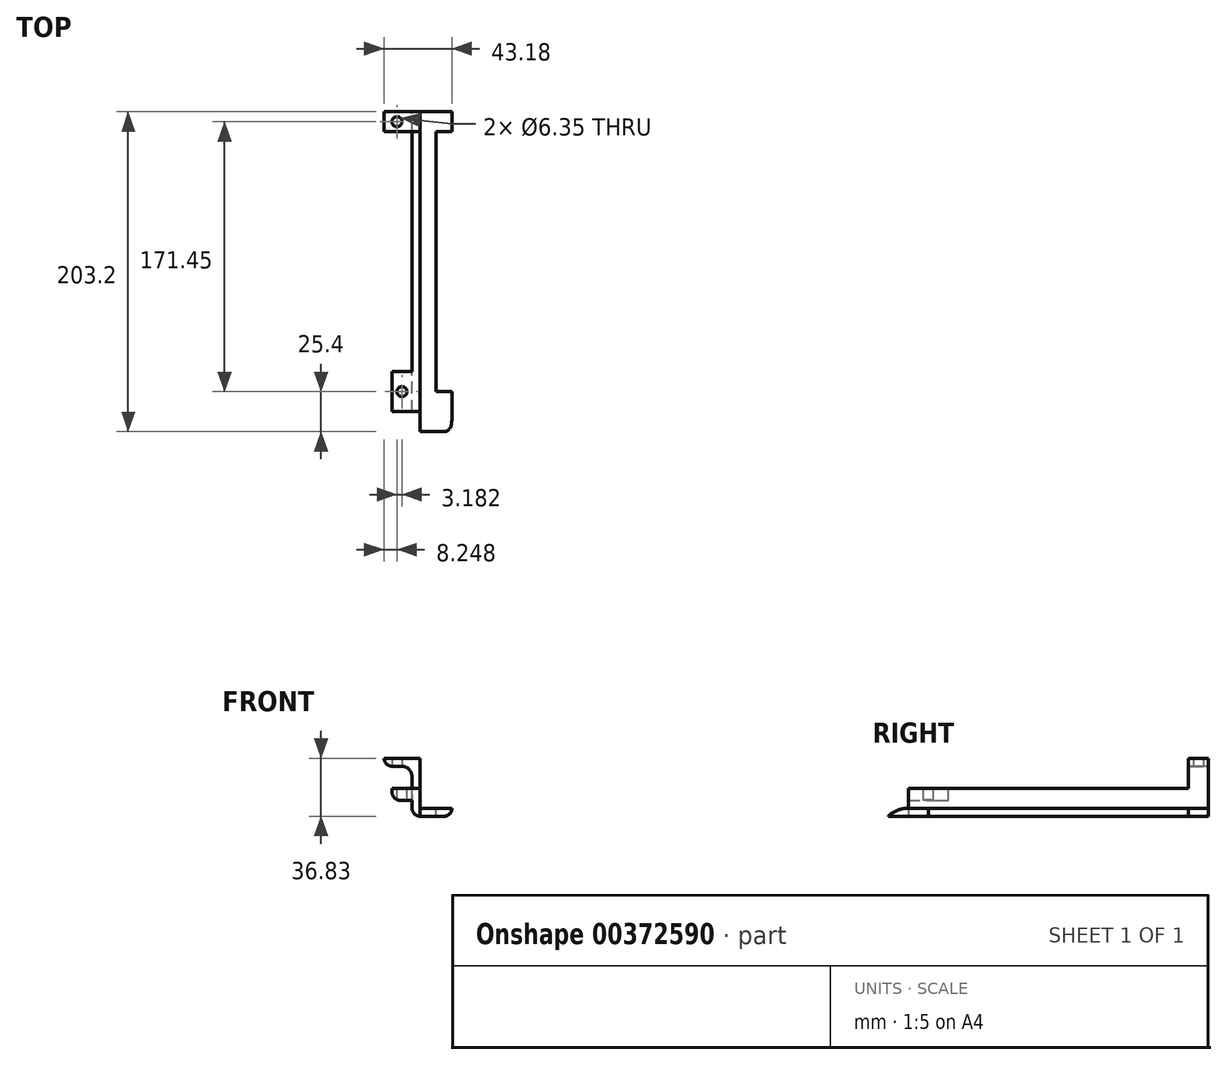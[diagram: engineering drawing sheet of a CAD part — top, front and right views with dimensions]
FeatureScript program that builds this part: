
annotation { "Feature Type Name" : "Feature", "Feature Type Description" : "" }
export const myFeature = defineFeature(function(context is Context, id is Id, definition is map)
    precondition{}
    {
        {
            var Q0;
            Q0=qCreatedBy(makeId("Right.planeOp"),FACE);
            var sketch = newSketch(context, id + "F0", { "sketchPlane" : qUnion([Q0])});
            skLineSegment(sketch, "E0", {"start": v(0, 0) * mm, "end": v(95.25, 0) * mm});
            skLineSegment(sketch, "E1", {"start": v(0, -12.7) * mm, "end": v(0, -6.35) * mm});
            skLineSegment(sketch, "E2", {"start": v(0, -12.7) * mm, "end": v(0, -17.78) * mm});
            skLineSegment(sketch, "E3", {"start": v(0, -17.78) * mm, "end": v(95.25, -17.78) * mm});
            skLineSegment(sketch, "E4", {"start": v(0, -12.7) * mm, "end": v(95.25, -12.7) * mm});
            skLineSegment(sketch, "E5", {"start": v(0, 0) * mm, "end": v(0, -6.35) * mm});
            skLineSegment(sketch, "E6", {"start": v(0, -25.4) * mm, "end": v(0, -12.7) * mm});
            skPoint(sketch, "E7.visualSharp", {"position": v(0, -6.35) * mm});
            skLineSegment(sketch, "E8", {"start": v(95.25, 0) * mm, "end": v(95.25, -17.78) * mm});
            skLineSegment(sketch, "E9.MirrorCS", {"start": v(190.5, 0) * mm, "end": v(95.25, 0) * mm});
            skLineSegment(sketch, "E10.MirrorCS", {"start": v(190.5, 0) * mm, "end": v(190.5, -6.35) * mm});
            skLineSegment(sketch, "E11.MirrorCS", {"start": v(190.5, -12.7) * mm, "end": v(190.5, -6.35) * mm});
            skLineSegment(sketch, "E12.MirrorCS", {"start": v(190.5, -12.7) * mm, "end": v(95.25, -12.7) * mm});
            skLineSegment(sketch, "E13.MirrorCS", {"start": v(190.5, -12.7) * mm, "end": v(190.5, -17.78) * mm});
            skLineSegment(sketch, "E14.MirrorCS", {"start": v(190.5, -17.78) * mm, "end": v(95.25, -17.78) * mm});
            skPoint(sketch, "E15.MirrorCS.start.orphan", {"position": v(190.5, 0) * mm});
            skPoint(sketch, "E16.MirrorCS.start.orphan", {"position": v(190.5, -25.4) * mm});
            skSolve(sketch);
        }
        {
            var Q0;
            {var subQ2=sQuery(id+"F0.wireOp",EDGE,"E0");Q0=makeQuery(id+"F0.imprint","IMPRINT",FACE,{"disambiguationData":[TD([[makeQuery(id+"F0.imprint","IMPRINT",EDGE,{"derivedFrom":subQ2}),-1.0]])]});}
            var Q1;
            Q1=makeQuery(id+"F0.imprint","IMPRINT",FACE,{"disambiguationData":[TD([[makeQuery(id+"F0.imprint","IMPRINT",EDGE,{"derivedFrom":sQuery(id+"F0.wireOp",EDGE,"E1")}),1.0]])]});
            var Q2;
            {var subQ0=sQuery(id+"F0.wireOp",EDGE,"E9.MirrorCS");Q2=makeQuery(id+"F0.imprint","IMPRINT",FACE,{"disambiguationData":[TD([[makeQuery(id+"F0.imprint","IMPRINT",EDGE,{"derivedFrom":subQ0}),1.0]])]});}
            var Q3;
            Q3=makeQuery(id+"F0.imprint","IMPRINT",FACE,{"disambiguationData":[TD([[makeQuery(id+"F0.imprint","IMPRINT",EDGE,{"derivedFrom":sQuery(id+"F0.wireOp",EDGE,"E15.MirrorCS")}),-1.0]])]});
            extrude(context, id + "F1", {"entities" : qUnion([Q0, Q1, Q2, Q3]), "depth" : 5.08 * mm});
        }
        {
            var Q0;
            Q0=makeQuery(id+"F0.imprint","IMPRINT",FACE,{"disambiguationData":[TD([[makeQuery(id+"F0.imprint","IMPRINT",EDGE,{"derivedFrom":sQuery(id+"F0.wireOp",EDGE,"E2")}),1.0]])]});
            var Q1;
            {var subQ2=sQuery(id+"F0.wireOp",EDGE,"E12.MirrorCS");Q1=makeQuery(id+"F0.imprint","IMPRINT",FACE,{"disambiguationData":[TD([[makeQuery(id+"F0.imprint","IMPRINT",EDGE,{"derivedFrom":subQ2}),1.0]])]});}
            var Q2;
            {var subQ0=sQuery(id+"F0.wireOp",EDGE,"E3");Q2=makeQuery(id+"F0.imprint","IMPRINT",FACE,{"disambiguationData":[TD([[makeQuery(id+"F0.imprint","IMPRINT",EDGE,{"derivedFrom":subQ0}),1.0]])]});}
            extrude(context, id + "F2", {"entities" : qUnion([Q0, Q1, Q2]), "operationType" : NewBodyOperationType.ADD, "depth" : 25.4 * mm});
        }
        {
            var Q0;
            {var subQ1=sQuery(id+"F0.wireOp",EDGE,"E0");Q0=makeQuery(id+"F0.imprint","IMPRINT",FACE,{"disambiguationData":[TD([[makeQuery(id+"F0.imprint","IMPRINT",EDGE,{"derivedFrom":subQ1}),-1.0]])]});}
            var sketch = newSketch(context, id + "F3", { "sketchPlane" : qUnion([Q0])});
            skLineSegment(sketch, "E17.bottom", {"start": v(0, 0) * mm, "end": v(50.8, 0) * mm});
            skLineSegment(sketch, "E17.top", {"start": v(0, -7.62) * mm, "end": v(50.8, -7.62) * mm});
            skLineSegment(sketch, "E17.left", {"start": v(0, 0) * mm, "end": v(0, -7.62) * mm});
            skLineSegment(sketch, "E17.right", {"start": v(50.8, 0) * mm, "end": v(50.8, -7.62) * mm});
            skSolve(sketch);
        }
        {
            var Q0;
            Q0=makeQuery(id+"F3.imprint","IMPRINT",FACE,{"disambiguationData":[TD([[makeQuery(id+"F3.imprint","IMPRINT",EDGE,{"derivedFrom":sQuery(id+"F3.wireOp",EDGE,"E17.bottom")}),-1.0]])]});
            extrude(context, id + "F4", {"entities" : qUnion([Q0]), "operationType" : NewBodyOperationType.ADD, "oppositeDirection" : true, "depth" : 12.7 * mm});
        }
        {
            var Q0;
            Q0=makeQuery(id+"F2.opExtrude","CAP_EDGE",EDGE,{"disambiguationData":[OSD([sQuery(id+"F0.wireOp",EDGE,"E3"),sQuery(id+"F0.wireOp",EDGE,"E14.MirrorCS")])],"isStart":true});
            var Q1;
            Q1=makeQuery(id+"F2.opExtrude","CAP_EDGE",EDGE,{"disambiguationData":[OSD([sQuery(id+"F0.wireOp",EDGE,"E3"),sQuery(id+"F0.wireOp",EDGE,"E14.MirrorCS")])],"isStart":false});
            var Q2;
            Q2=makeQuery(id+"F4.opExtrude","CAP_EDGE",EDGE,{"disambiguationData":[OSD([sQuery(id+"F3.wireOp",EDGE,"E17.top")])],"isStart":false});
            fillet(context, id + "F5", {"entities" : qUnion([Q0, Q1, Q2]), "radius" : 5.08 * mm, "tangentPropagation" : true, "allowEdgeOverflow" : false});
        }
        {
            var Q0;
            Q0=makeQuery(id+"F4.boolean.opBoolean","MERGE",FACE,{"derivedFrom":[makeQuery(id+"F1.opExtrude","SWEPT_FACE",FACE,{"disambiguationData":[OSD([sQuery(id+"F0.wireOp",EDGE,"E0"),sQuery(id+"F0.wireOp",EDGE,"E9.MirrorCS")])]}),makeQuery(id+"F4.opExtrude","SWEPT_FACE",FACE,{"disambiguationData":[OSD([sQuery(id+"F3.wireOp",EDGE,"E17.bottom")])]})]});
            var sketch = newSketch(context, id + "F6", { "sketchPlane" : qUnion([Q0])});
            skLineSegment(sketch, "E18", {"start": v(5.08, 0) * mm, "end": v(-12.7, 0) * mm});
            skLineSegment(sketch, "E19", {"start": v(-12.7, 0) * mm, "end": v(0, 0) * mm});
            skLineSegment(sketch, "E20", {"start": v(0, 0) * mm, "end": v(0, 50.8) * mm});
            skLineSegment(sketch, "E21", {"start": v(0, 50.8) * mm, "end": v(-12.7, 50.8) * mm});
            skLineSegment(sketch, "E22", {"start": v(-6.35, 50.8) * mm, "end": v(-6.35, 0) * mm});
            skLineSegment(sketch, "E23", {"start": v(-6.35, 25.4) * mm, "end": v(0, 25.4) * mm});
            skLineSegment(sketch, "E24", {"start": v(-6.35, 25.4) * mm, "end": v(-6.35, 0) * mm});
            skLineSegment(sketch, "E25", {"start": v(-6.35, 25.4) * mm, "end": v(-6.35, 38.1) * mm});
            skPoint(sketch, "E26", {"position": v(-6.35, 38.1) * mm});
            skPoint(sketch, "E27", {"position": v(-6.35, 12.7) * mm});
            skLineSegment(sketch, "E28", {"start": v(-6.35, 25.4) * mm, "end": v(-12.7, 25.4) * mm});
            skSolve(sketch);
        }
        {
            var Q0;
            Q0=sQuery(id+"F6.wireOp",VERTEX,"E27");
            var Q1;
            Q1=sQuery(id+"F6.wireOp",VERTEX,"E26");
            var Q2;
            Q2=makeQuery(id+"F1.opExtrude","SWEPT_BODY",BODY,{"disambiguationData":[OSD([sQuery(id+"F0.wireOp",EDGE,"E0"),sQuery(id+"F0.wireOp",EDGE,"E1"),sQuery(id+"F0.wireOp",EDGE,"E4"),sQuery(id+"F0.wireOp",EDGE,"E5"),sQuery(id+"F0.wireOp",EDGE,"E9.MirrorCS"),sQuery(id+"F0.wireOp",EDGE,"E10.MirrorCS"),sQuery(id+"F0.wireOp",EDGE,"E11.MirrorCS"),sQuery(id+"F0.wireOp",EDGE,"E12.MirrorCS")])]});
            hole(context, id + "F7", {"style" : HoleStyle.SIMPLE, "endStyle" : HoleEndStyle.THROUGH, "holeDiameter" : 6.35 * mm, "isTappedThrough" : true, "tappedDepth" : 12.7 * mm, "tapClearance" : 3, "locations" : qUnion([Q0, Q1]), "scope" : qUnion([Q2])});
        }
        {
            var Q0;
            Q0=makeQuery(id+"F4.boolean.opBoolean","MERGE",FACE,{"derivedFrom":[makeQuery(id+"F1.opExtrude","SWEPT_FACE",FACE,{"disambiguationData":[OSD([sQuery(id+"F0.wireOp",EDGE,"E0"),sQuery(id+"F0.wireOp",EDGE,"E9.MirrorCS")])]}),makeQuery(id+"F4.opExtrude","SWEPT_FACE",FACE,{"disambiguationData":[OSD([sQuery(id+"F3.wireOp",EDGE,"E17.bottom")])]})]});
            var sketch = newSketch(context, id + "F8", { "sketchPlane" : qUnion([Q0])});
            skSolve(sketch);
        }
        {
            var Q0;
            {var subQ0=sQuery(id+"F3.wireOp",EDGE,"E17.bottom");Q0=makeQuery(id+"F8.imprint","IMPRINT",FACE,{"disambiguationData":[TD([[makeQuery(id+"F8.imprint","IMPRINT",EDGE,{"derivedFrom":makeQuery(id+"F4.opExtrude","CAP_EDGE",EDGE,{"disambiguationData":[OSD([subQ0])],"isStart":false})}),-1.0]])]});}
            var sketch = newSketch(context, id + "F9", { "sketchPlane" : qUnion([Q0])});
            skLineSegment(sketch, "E29.bottom", {"start": v(0, 0) * mm, "end": v(8.89, 0) * mm});
            skLineSegment(sketch, "E29.top", {"start": v(0, 190.5) * mm, "end": v(8.89, 190.5) * mm});
            skLineSegment(sketch, "E29.left", {"start": v(0, 0) * mm, "end": v(0, 190.5) * mm});
            skLineSegment(sketch, "E29.right", {"start": v(8.89, 0) * mm, "end": v(8.89, 190.5) * mm});
            skLineSegment(sketch, "E30", {"start": v(8.89, 190.5) * mm, "end": v(8.89, 177.8) * mm});
            skLineSegment(sketch, "E31", {"start": v(8.89, 177.8) * mm, "end": v(0, 177.8) * mm});
            skSolve(sketch);
        }
        {
            var Q0;
            {var subQ0=sQuery(id+"F9.wireOp",EDGE,"E29.top");Q0=makeQuery(id+"F9.imprint","IMPRINT",FACE,{"disambiguationData":[TD([[makeQuery(id+"F9.imprint","IMPRINT",EDGE,{"derivedFrom":subQ0}),1.0]])]});}
            extrude(context, id + "F10", {"entities" : qUnion([Q0]), "operationType" : NewBodyOperationType.ADD, "depth" : 19.05 * mm});
        }
        {
            var Q0;
            {var subQ0=sQuery(id+"F0.wireOp",EDGE,"E12.MirrorCS");var subQ1=sQuery(id+"F0.wireOp",EDGE,"E4");Q0=makeQuery(id+"F10.boolean.opBoolean","MERGE",FACE,{"derivedFrom":[makeQuery(id+"F2.boolean.opBoolean","MERGE",FACE,{"derivedFrom":[makeQuery(id+"F1.opExtrude","CAP_FACE",FACE,{"disambiguationData":[OSD([sQuery(id+"F0.wireOp",EDGE,"E0"),sQuery(id+"F0.wireOp",EDGE,"E1"),subQ1,sQuery(id+"F0.wireOp",EDGE,"E5"),sQuery(id+"F0.wireOp",EDGE,"E9.MirrorCS"),sQuery(id+"F0.wireOp",EDGE,"E10.MirrorCS"),sQuery(id+"F0.wireOp",EDGE,"E11.MirrorCS"),subQ0])],"isStart":true}),makeQuery(id+"F2.opExtrude","CAP_FACE",FACE,{"disambiguationData":[OSD([sQuery(id+"F0.wireOp",EDGE,"E3"),subQ1,sQuery(id+"F0.wireOp",EDGE,"E6"),subQ0,sQuery(id+"F0.wireOp",EDGE,"E13.MirrorCS"),sQuery(id+"F0.wireOp",EDGE,"E14.MirrorCS")])],"isStart":true})]}),makeQuery(id+"F10.opExtrude","SWEPT_FACE",FACE,{"disambiguationData":[OSD([sQuery(id+"F9.wireOp",EDGE,"E29.left")])]})]});}
            var sketch = newSketch(context, id + "F11", { "sketchPlane" : qUnion([Q0])});
            skLineSegment(sketch, "E32.bottom", {"start": v(-190.5, 19.05) * mm, "end": v(-177.8, 19.05) * mm});
            skLineSegment(sketch, "E32.top", {"start": v(-190.5, 13.97) * mm, "end": v(-177.8, 13.97) * mm});
            skLineSegment(sketch, "E32.left", {"start": v(-190.5, 19.05) * mm, "end": v(-190.5, 13.97) * mm});
            skLineSegment(sketch, "E32.right", {"start": v(-177.8, 19.05) * mm, "end": v(-177.8, 13.97) * mm});
            skSolve(sketch);
        }
        {
            var Q0;
            Q0 = qSketchRegion(id + "F11", true);
            extrude(context, id + "F12", {"entities" : qUnion([Q0]), "operationType" : NewBodyOperationType.ADD, "depth" : 17.78 * mm});
        }
        {
            var Q0;
            Q0=makeQuery(id+"F12.boolean.opBoolean","MERGE",FACE,{"derivedFrom":[makeQuery(id+"F10.opExtrude","CAP_FACE",FACE,{"disambiguationData":[OSD([sQuery(id+"F9.wireOp",EDGE,"E29.top"),sQuery(id+"F9.wireOp",EDGE,"E29.left"),sQuery(id+"F9.wireOp",EDGE,"E30"),sQuery(id+"F9.wireOp",EDGE,"E31")])],"isStart":false}),makeQuery(id+"F12.opExtrude","SWEPT_FACE",FACE,{"disambiguationData":[OSD([sQuery(id+"F11.wireOp",EDGE,"E32.bottom")])]})]});
            var sketch = newSketch(context, id + "F13", { "sketchPlane" : qUnion([Q0])});
            skLineSegment(sketch, "E33", {"start": v(5.08, 184.15) * mm, "end": v(-17.78, 184.15) * mm});
            skPoint(sketch, "E34", {"position": v(-6.35, 184.15) * mm});
            skLineSegment(sketch, "E35", {"start": v(-6.35, 184.15) * mm, "end": v(-17.78, 184.15) * mm});
            skPoint(sketch, "E36", {"position": v(-12.06, 184.15) * mm});
            skLineSegment(sketch, "E37", {"start": v(-6.35, 184.15) * mm, "end": v(-12.06, 184.15) * mm});
            skPoint(sketch, "E38", {"position": v(-9.2, 184.15) * mm});
            skSolve(sketch);
        }
        {
            var Q0;
            Q0=sQuery(id+"F13.wireOp",VERTEX,"E38");
            var Q1;
            Q1=makeQuery(id+"F1.opExtrude","SWEPT_BODY",BODY,{"disambiguationData":[OSD([sQuery(id+"F0.wireOp",EDGE,"E0"),sQuery(id+"F0.wireOp",EDGE,"E1"),sQuery(id+"F0.wireOp",EDGE,"E4"),sQuery(id+"F0.wireOp",EDGE,"E5"),sQuery(id+"F0.wireOp",EDGE,"E9.MirrorCS"),sQuery(id+"F0.wireOp",EDGE,"E10.MirrorCS"),sQuery(id+"F0.wireOp",EDGE,"E11.MirrorCS"),sQuery(id+"F0.wireOp",EDGE,"E12.MirrorCS")])]});
            hole(context, id + "F14", {"style" : HoleStyle.SIMPLE, "endStyle" : HoleEndStyle.THROUGH, "holeDiameter" : 6.35 * mm, "isTappedThrough" : true, "tappedDepth" : 12.7 * mm, "tapClearance" : 3, "locations" : qUnion([Q0]), "scope" : qUnion([Q1])});
        }
        {
            var Q0;
            Q0=makeQuery(id+"F12.boolean.opBoolean","MERGE",FACE,{"derivedFrom":[makeQuery(id+"F10.boolean.opBoolean","MERGE",FACE,{"derivedFrom":[makeQuery(id+"F2.boolean.opBoolean","MERGE",FACE,{"derivedFrom":[makeQuery(id+"F1.opExtrude","SWEPT_FACE",FACE,{"disambiguationData":[OSD([sQuery(id+"F0.wireOp",EDGE,"E10.MirrorCS"),sQuery(id+"F0.wireOp",EDGE,"E11.MirrorCS")])]}),makeQuery(id+"F2.opExtrude","SWEPT_FACE",FACE,{"disambiguationData":[OSD([sQuery(id+"F0.wireOp",EDGE,"E13.MirrorCS")])]})]}),makeQuery(id+"F10.opExtrude","SWEPT_FACE",FACE,{"disambiguationData":[OSD([sQuery(id+"F9.wireOp",EDGE,"E29.top")])]})]}),makeQuery(id+"F12.opExtrude","SWEPT_FACE",FACE,{"disambiguationData":[OSD([sQuery(id+"F11.wireOp",EDGE,"E32.left")])]})]});
            var sketch = newSketch(context, id + "F15", { "sketchPlane" : qUnion([Q0])});
            skLineSegment(sketch, "E39", {"start": v(17.78, 19.05) * mm, "end": v(17.78, 13.97) * mm});
            skLineSegment(sketch, "E40", {"start": v(17.78, 13.97) * mm, "end": v(6.35, 13.97) * mm});
            skLineSegment(sketch, "E41", {"start": v(0, 7.62) * mm, "end": v(0, 0) * mm});
            skLineSegment(sketch, "E42", {"start": v(0, 0) * mm, "end": v(-5.08, 0) * mm});
            skLineSegment(sketch, "E43", {"start": v(-5.08, 0) * mm, "end": v(-5.08, 19.05) * mm});
            skLineSegment(sketch, "E44", {"start": v(-5.08, 19.05) * mm, "end": v(17.78, 19.05) * mm});
            skPoint(sketch, "E45.visualSharp", {"position": v(0, 13.97) * mm});
            skArc(sketch, "E45.filletArc", {"start": v(6.35, 13.97) * mm, "mid": v(1.86, 12.11) * mm, "end": v(0, 7.62) * mm});
            skSolve(sketch);
        }
        {
            var Q0;
            Q0 = qSketchRegion(id + "F15", true);
            extrude(context, id + "F16", {"entities" : qUnion([Q0]), "operationType" : NewBodyOperationType.ADD, "oppositeDirection" : true, "depth" : 12.7 * mm});
        }
        {
            var Q0;
            Q0=makeQuery(id+"F16.boolean.opBoolean","MERGE",FACE,{"derivedFrom":[makeQuery(id+"F12.opExtrude","SWEPT_FACE",FACE,{"disambiguationData":[OSD([sQuery(id+"F11.wireOp",EDGE,"E32.top")])]}),makeQuery(id+"F16.opExtrude","SWEPT_FACE",FACE,{"disambiguationData":[OSD([sQuery(id+"F15.wireOp",EDGE,"E40")])]})]});
            var sketch = newSketch(context, id + "F17", { "sketchPlane" : qUnion([Q0])});
            skLineSegment(sketch, "E46", {"start": v(-6.35, -177.8) * mm, "end": v(-17.78, -177.8) * mm});
            skLineSegment(sketch, "E47", {"start": v(-17.78, -177.8) * mm, "end": v(-12.07, -177.8) * mm});
            skLineSegment(sketch, "E48", {"start": v(-12.07, -177.8) * mm, "end": v(-12.07, -190.5) * mm});
            skPoint(sketch, "E49", {"position": v(-12.07, -184.15) * mm});
            skLineSegment(sketch, "E50", {"start": v(-12.07, -184.15) * mm, "end": v(-9.53, -184.15) * mm});
            skPoint(sketch, "E51", {"position": v(-9.53, -184.15) * mm});
            skSolve(sketch);
        }
        {
            var Q0;
            Q0=sQuery(id+"F17.wireOp",VERTEX,"E51");
            var Q1;
            Q1=makeQuery(id+"F1.opExtrude","SWEPT_BODY",BODY,{"disambiguationData":[OSD([sQuery(id+"F0.wireOp",EDGE,"E0"),sQuery(id+"F0.wireOp",EDGE,"E1"),sQuery(id+"F0.wireOp",EDGE,"E4"),sQuery(id+"F0.wireOp",EDGE,"E5"),sQuery(id+"F0.wireOp",EDGE,"E9.MirrorCS"),sQuery(id+"F0.wireOp",EDGE,"E10.MirrorCS"),sQuery(id+"F0.wireOp",EDGE,"E11.MirrorCS"),sQuery(id+"F0.wireOp",EDGE,"E12.MirrorCS")])]});
            hole(context, id + "F18", {"style" : HoleStyle.SIMPLE, "endStyle" : HoleEndStyle.THROUGH, "holeDiameter" : 6.35 * mm, "isTappedThrough" : true, "tappedDepth" : 12.7 * mm, "tapClearance" : 3, "locations" : qUnion([Q0]), "scope" : qUnion([Q1])});
        }
        {
            var Q0;
            Q0=makeQuery(id+"F12.opExtrude","CAP_EDGE",EDGE,{"disambiguationData":[OSD([sQuery(id+"F11.wireOp",EDGE,"E32.top")])],"isStart":false});
            fillet(context, id + "F19", {"entities" : qUnion([Q0]), "radius" : 5.08 * mm, "tangentPropagation" : true, "allowEdgeOverflow" : false});
        }
        {
            var Q0;
            Q0=makeQuery(id+"F2.opExtrude","SWEPT_FACE",FACE,{"disambiguationData":[OSD([sQuery(id+"F0.wireOp",EDGE,"E4"),sQuery(id+"F0.wireOp",EDGE,"E12.MirrorCS")])]});
            var sketch = newSketch(context, id + "F20", { "sketchPlane" : qUnion([Q0])});
            skLineSegment(sketch, "E52", {"start": v(25.4, 0) * mm, "end": v(25.4, 190.5) * mm});
            skLineSegment(sketch, "E53", {"start": v(25.4, 190.5) * mm, "end": v(5.08, 190.5) * mm});
            skLineSegment(sketch, "E54", {"start": v(5.08, 190.5) * mm, "end": v(5.08, 0) * mm});
            skLineSegment(sketch, "E55", {"start": v(5.08, 0) * mm, "end": v(25.4, 0) * mm});
            skLineSegment(sketch, "E56", {"start": v(5.08, 190.5) * mm, "end": v(5.08, 177.8) * mm});
            skLineSegment(sketch, "E57", {"start": v(5.08, 177.8) * mm, "end": v(25.4, 177.8) * mm});
            skLineSegment(sketch, "E58", {"start": v(25.4, 0) * mm, "end": v(25.4, 12.7) * mm});
            skLineSegment(sketch, "E59", {"start": v(25.4, 12.7) * mm, "end": v(5.08, 12.7) * mm});
            skLineSegment(sketch, "E60", {"start": v(15.24, 12.7) * mm, "end": v(15.24, 177.8) * mm});
            skSolve(sketch);
        }
        {
            var Q0;
            {var subQ5=sQuery(id+"F20.wireOp",EDGE,"E60");Q0=makeQuery(id+"F20.imprint","IMPRINT",FACE,{"disambiguationData":[TD([[makeQuery(id+"F20.imprint","IMPRINT",EDGE,{"derivedFrom":subQ5}),-1.0]])]});}
            extrude(context, id + "F21", {"entities" : qUnion([Q0]), "operationType" : NewBodyOperationType.REMOVE, "oppositeDirection" : true, "depth" : 25.4 * mm});
        }
        {
            var Q0;
            {var subQ1=sQuery(id+"F6.wireOp",EDGE,"E22");Q0=makeQuery(id+"F6.imprint","IMPRINT",FACE,{"disambiguationData":[TD([[makeQuery(id+"F6.imprint","IMPRINT",EDGE,{"derivedFrom":subQ1}),-1.0]])]});}
            var Q1;
            {var subQ1=sQuery(id+"F6.wireOp",EDGE,"E22");Q1=makeQuery(id+"F6.imprint","IMPRINT",FACE,{"disambiguationData":[TD([[makeQuery(id+"F6.imprint","IMPRINT",EDGE,{"derivedFrom":subQ1}),1.0]])]});}
            extrude(context, id + "F22", {"entities" : qUnion([Q0, Q1]), "operationType" : NewBodyOperationType.REMOVE, "oppositeDirection" : true, "depth" : 25.4 * mm});
        }
        {
            var Q0;
            Q0=makeQuery(id+"F4.boolean.opBoolean","MERGE",FACE,{"derivedFrom":[makeQuery(id+"F2.boolean.opBoolean","MERGE",FACE,{"derivedFrom":[makeQuery(id+"F1.opExtrude","SWEPT_FACE",FACE,{"disambiguationData":[OSD([sQuery(id+"F0.wireOp",EDGE,"E1"),sQuery(id+"F0.wireOp",EDGE,"E5")])]}),makeQuery(id+"F2.opExtrude","SWEPT_FACE",FACE,{"disambiguationData":[OSD([sQuery(id+"F0.wireOp",EDGE,"E6")])]})]}),makeQuery(id+"F4.opExtrude","SWEPT_FACE",FACE,{"disambiguationData":[OSD([sQuery(id+"F3.wireOp",EDGE,"E17.left")])]})]});
            var sketch = newSketch(context, id + "F23", { "sketchPlane" : qUnion([Q0])});
            skLineSegment(sketch, "E61", {"start": v(5.08, -12.7) * mm, "end": v(5.08, -17.78) * mm});
            skLineSegment(sketch, "E62", {"start": v(5.08, -12.7) * mm, "end": v(25.4, -12.7) * mm});
            skLineSegment(sketch, "E63", {"start": v(25.4, -12.7) * mm, "end": v(25.4, -17.78) * mm});
            skLineSegment(sketch, "E64", {"start": v(25.4, -17.78) * mm, "end": v(5.08, -17.78) * mm});
            skSolve(sketch);
        }
        {
            var Q0;
            {var subQ0=sQuery(id+"F23.wireOp",EDGE,"E61");Q0=makeQuery(id+"F23.imprint","IMPRINT",FACE,{"disambiguationData":[TD([[makeQuery(id+"F23.imprint","IMPRINT",EDGE,{"derivedFrom":subQ0}),1.0]])]});}
            extrude(context, id + "F24", {"entities" : qUnion([Q0]), "operationType" : NewBodyOperationType.ADD, "depth" : 12.7 * mm});
        }
        {
            var Q0;
            Q0=makeQuery(id+"F24.opExtrude","CAP_EDGE",EDGE,{"disambiguationData":[OSD([sQuery(id+"F23.wireOp",EDGE,"E62")])],"isStart":false});
            fillet(context, id + "F25", {"entities" : qUnion([Q0]), "radius" : 18.4 * mm, "tangentPropagation" : true, "allowEdgeOverflow" : false});
        }
    });
